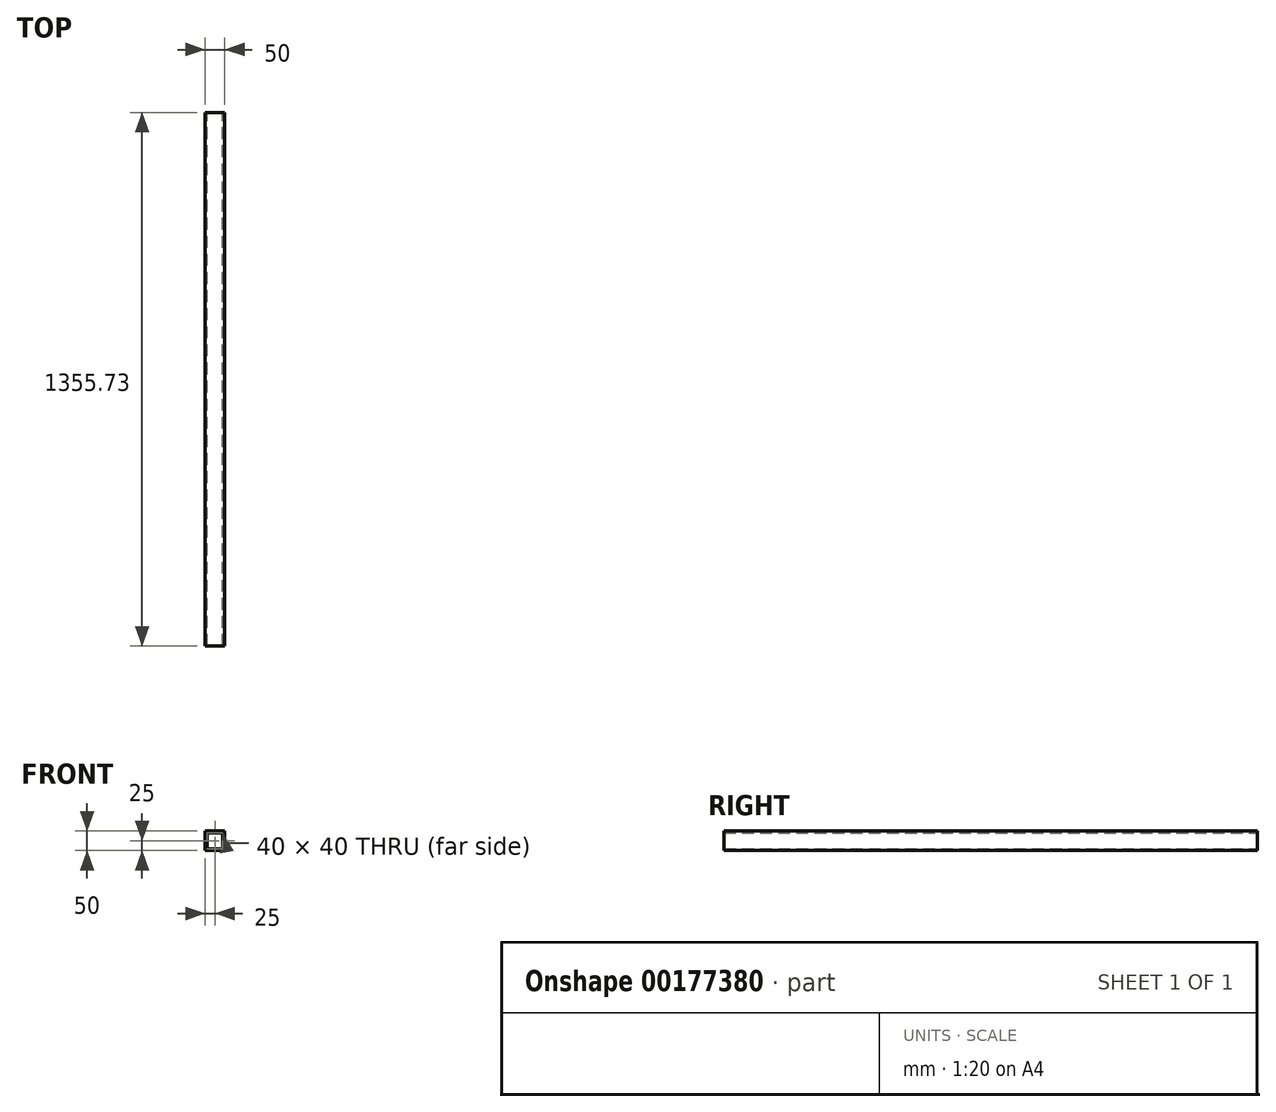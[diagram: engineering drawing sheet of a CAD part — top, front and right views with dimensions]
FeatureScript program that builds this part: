
annotation { "Feature Type Name" : "Feature", "Feature Type Description" : "" }
export const myFeature = defineFeature(function(context is Context, id is Id, definition is map)
    precondition{}
    {
        {
            var Q0;
            Q0=qCreatedBy(makeId("Front.planeOp"),FACE);
            var sketch = newSketch(context, id + "F0", { "sketchPlane" : qUnion([Q0])});
            skLineSegment(sketch, "E0.bottom", {"start": v(25, -25) * mm, "end": v(-25, -25) * mm});
            skLineSegment(sketch, "E0.top", {"start": v(25, 25) * mm, "end": v(-25, 25) * mm});
            skLineSegment(sketch, "E0.left", {"start": v(25, -25) * mm, "end": v(25, 25) * mm});
            skLineSegment(sketch, "E0.right", {"start": v(-25, -25) * mm, "end": v(-25, 25) * mm});
            skPoint(sketch, "E0.middle", {"position": v(0, 0) * mm});
            skLineSegment(sketch, "E1.0", {"start": v(20, 20) * mm, "end": v(-20, 20) * mm});
            skLineSegment(sketch, "E1.1", {"start": v(20, -20) * mm, "end": v(20, 20) * mm});
            skLineSegment(sketch, "E1.2", {"start": v(20, -20) * mm, "end": v(-20, -20) * mm});
            skLineSegment(sketch, "E1.3", {"start": v(-20, -20) * mm, "end": v(-20, 20) * mm});
            skSolve(sketch);
        }
        {
            var Q0;
            Q0=makeQuery(id+"F0.imprint","IMPRINT",FACE,{"disambiguationData":[TD([[makeQuery(id+"F0.imprint","IMPRINT",EDGE,{"derivedFrom":sQuery(id+"F0.wireOp",EDGE,"E0.bottom")}),-1.0]])]});
            extrude(context, id + "F1", {"entities" : qUnion([Q0]), "depth" : 1355.72 * mm});
        }
    });
